# Revit family: Toilet-Floor_Mount-KOHLER-REVE-K-17181T_1
name_source: partatom
category: Plumbing Fixtures
revit_build: Autodesk Revit 2017 (Build: 20160225_1515(x64)
units: mm (PartAtom-declared; Revit-internal decimal feet)

## family parameters
Cut with Voids When Loaded = No
Host = Face
OmniClass Number = 23.31.19.00
OmniClass Title = Toilets
Part Type = Normal
Room Calculation Point = No
Round Connector Dimension = Use Diameter
Shared = No

## types (3) — shared parameters
ADA Compliant = No
Assembly Code = D2010100
Bowl heigth = 16 1/16"
CW Connection = Yes
Cold Water Inlet = Cold Water Inlet
Date Modified = 06/25/2021
Default Elevation = 0"
Finish = Kohler-Vitreous_China-0-White
Flow Rate = 0 GPM
Flush Rate- GPF = 1.58 GPF
Flush Rate- LPF = 6LPF
HW Connection = No
Height = 27 7/8"
Hot Water Inlet = Hot Water Inlet
Length = 26 15/16"
Manufacturer = KOHLER Co.
Master Format 2014 = 22 42 13.13
Master Format 2014 Name = Residential Water Closets
Material = Vitreous China
Pressure = 0.00 psi
Product Name = REVE
Rough-In = 12"
Seat Included = Yes
URL = http://www.kohler.com.cn
Vent Connection = No
Waste Connection = Yes
Waste Water Outlet = Waste Water Outlet
WaterSense Certified = No
Width = 14 5/8"

## per-type parameters (varying)
| type | Connector Outlet Diameter 1 | Connector Outlet Diameter 2 | Description | Ground Drainage | Model | Product Page URL | Type | Wall Drainage |
| SP2-Wall Drainage,0-White | 2 1/8" | 0" | IPC TOILET  S-TRAP 3.5/6.0L | No | K-17181T-SP2-0 |  | 1 | Yes |
| S2-Ground Drainage,0-White | 0" | 2 1/8" | One-piece Toilet | Yes | K-17181T-S2-0 | https://www.kohler.com.cn | 2 | No |
| SBG2-Gold Series Ground Drainage,0-White | 0" | 2 1/8" | One-piece Toilet (Fashion Luxury Gold Series) | Yes | K-17181T-SBG2-0 | https://www.kohler.com.cn | 3 | No |

## geometry (parser evidence)
native form markers: Sweep x5
no freeform markers — native parametric forms only
